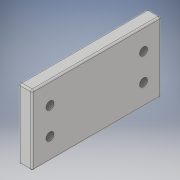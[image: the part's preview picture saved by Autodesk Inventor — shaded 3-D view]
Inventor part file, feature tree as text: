
AUTODESK INVENTOR PART (.ipt)
format: ipt  version: 2019 (Build 230136000, 136)  size: 130,560 bytes
history: native  units: in
note: dims shown in document units (in); Inventor stores cm internally (conversion verified against a paired STEP export)
features: extrude x2, mirror x2, thread x1, fillet x1, sketch x1
ambient origin geometry x8: Origin, YZ Plane, XZ Plane, XY Plane, X Axis, Y Axis, Z Axis, Center Point
bodies: Solid1 (feature_tree)
feature tree (7):
  extrude  "Extrusion1"  Depth=1.0236in
  extrude  "Extrusion2"  Depth=0.1969in TaperAngle=0.0deg
  thread  "Thread1"  [1 undecoded]
  mirror  "Mirror1"
  fillet  "Fillet1"  Radius=0.1181in
  mirror  "Mirror2"
  sketch  "Sketch1"  dims[d0=1.8898in d1=1.0236in d2=0.1969in d3=0.0in d5=0.1181in d6=0.1181in d7=0.0in d8=0.3937in d9=0.0in d10=0.0236in d11=0.6853in d12=0.1969in]
note: 1 required parameter value undecoded (feature->parameter linkage not recoverable at this tier; creation-order binding heuristic only, values carry confidence <= 0.55)
